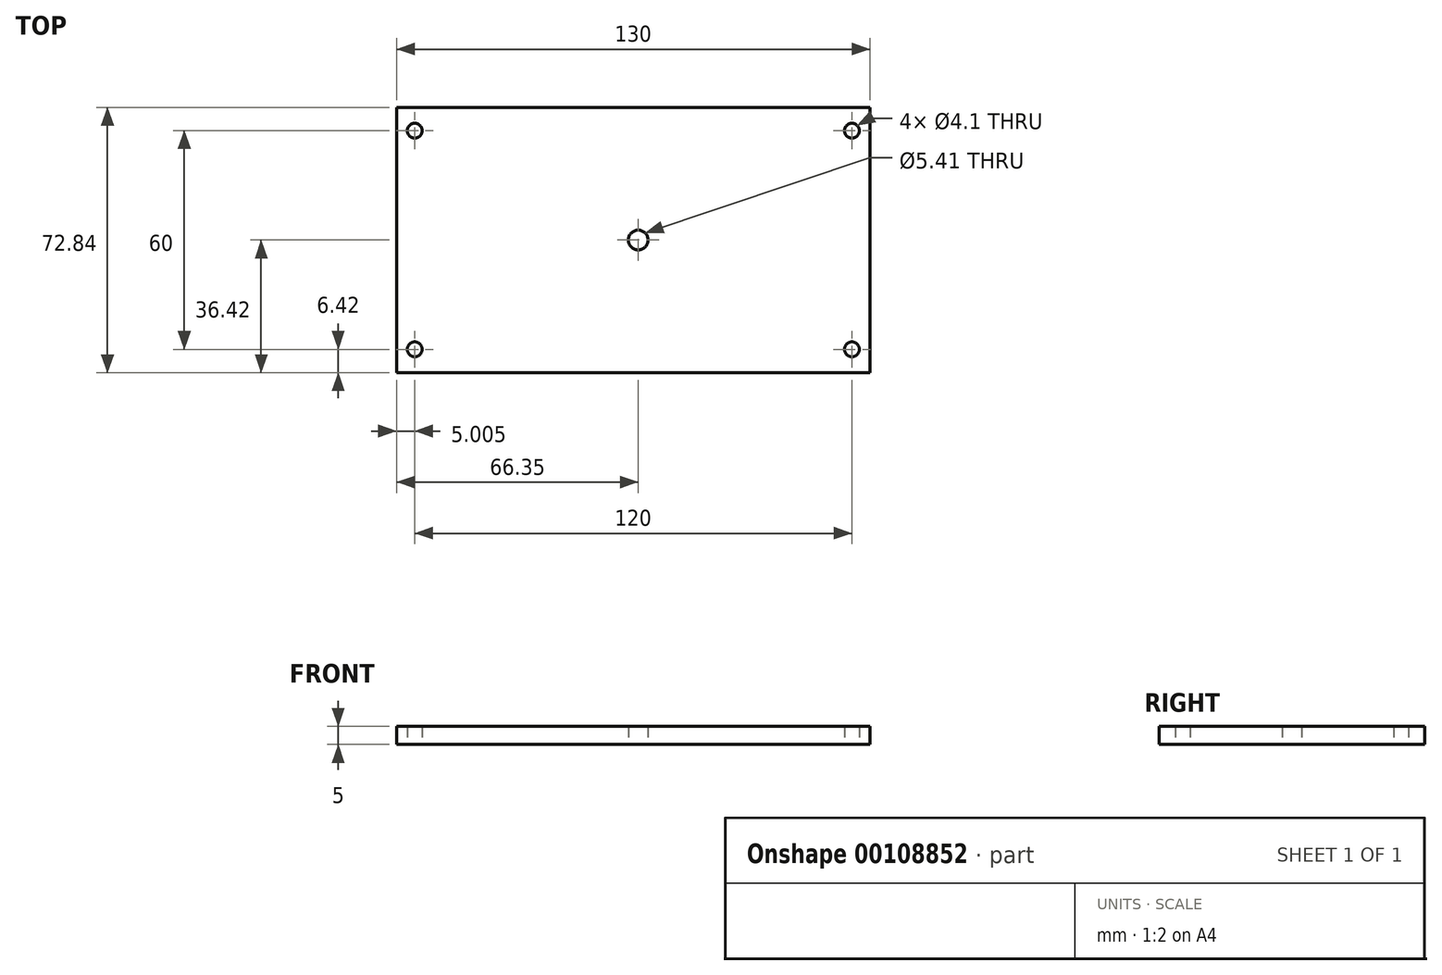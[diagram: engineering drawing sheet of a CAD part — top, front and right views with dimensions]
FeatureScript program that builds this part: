
annotation { "Feature Type Name" : "Feature", "Feature Type Description" : "" }
export const myFeature = defineFeature(function(context is Context, id is Id, definition is map)
    precondition{}
    {
        {
            var Q0;
            Q0=qCreatedBy(makeId("Top.planeOp"),FACE);
            var sketch = newSketch(context, id + "F0", { "sketchPlane" : qUnion([Q0])});
            skLineSegment(sketch, "E0", {"start": v(-72.88, 0) * mm, "end": v(75.67, 0) * mm, "construction": true});
            skLineSegment(sketch, "E1", {"start": v(0, 57.85) * mm, "end": v(0, -46.9) * mm, "construction": true});
            skLineSegment(sketch, "E2", {"start": v(-61.35, 34.24) * mm, "end": v(-61.35, -40.9) * mm, "construction": true});
            skLineSegment(sketch, "E3", {"start": v(58.65, 43.04) * mm, "end": v(58.65, -44.11) * mm, "construction": true});
            skLineSegment(sketch, "E4", {"start": v(-63.43, 30) * mm, "end": v(74.6, 30) * mm, "construction": true});
            skLineSegment(sketch, "E5", {"start": v(-63.43, -30) * mm, "end": v(67.94, -30) * mm, "construction": true});
            skPoint(sketch, "E6", {"position": v(-61.35, 30) * mm});
            skPoint(sketch, "E7", {"position": v(-61.35, -30) * mm});
            skPoint(sketch, "E8", {"position": v(58.65, -30) * mm});
            skPoint(sketch, "E9", {"position": v(58.65, 30) * mm});
            skLineSegment(sketch, "E10.bottom", {"start": v(-66.35, 0) * mm, "end": v(63.65, 0) * mm});
            skLineSegment(sketch, "E10.top", {"start": v(-66.35, 36.42) * mm, "end": v(63.65, 36.42) * mm});
            skLineSegment(sketch, "E10.left", {"start": v(-66.35, 0) * mm, "end": v(-66.35, 36.42) * mm});
            skLineSegment(sketch, "E10.right", {"start": v(63.65, 0) * mm, "end": v(63.65, 36.42) * mm});
            skLineSegment(sketch, "E11.MirrorCS", {"start": v(-66.35, -36.42) * mm, "end": v(63.65, -36.42) * mm});
            skLineSegment(sketch, "E12.MirrorCS", {"start": v(63.65, 0) * mm, "end": v(63.65, -36.42) * mm});
            skLineSegment(sketch, "E13.MirrorCS", {"start": v(-66.35, 0) * mm, "end": v(-66.35, -36.42) * mm});
            skPoint(sketch, "E14", {"position": v(0, 0) * mm});
            skSolve(sketch);
        }
        {
            var Q0;
            Q0 = qSketchRegion(id + "F0", true);
            extrude(context, id + "F1", {"entities" : qUnion([Q0]), "depth" : 5 * mm});
        }
        {
            var Q0;
            Q0=sQuery(id+"F0.wireOp",VERTEX,"E6");
            var Q1;
            Q1=sQuery(id+"F0.wireOp",VERTEX,"E7");
            var Q2;
            Q2=sQuery(id+"F0.wireOp",VERTEX,"E9");
            var Q3;
            Q3=sQuery(id+"F0.wireOp",VERTEX,"E8");
            var Q4;
            Q4=makeQuery(id+"F1.opExtrude","SWEPT_BODY",BODY,{"disambiguationData":[OSD([sQuery(id+"F0.wireOp",EDGE,"E10.top"),sQuery(id+"F0.wireOp",EDGE,"E10.left"),sQuery(id+"F0.wireOp",EDGE,"E10.right"),sQuery(id+"F0.wireOp",EDGE,"E11.MirrorCS"),sQuery(id+"F0.wireOp",EDGE,"E12.MirrorCS"),sQuery(id+"F0.wireOp",EDGE,"E13.MirrorCS")])]});
            hole(context, id + "F2", {"style" : HoleStyle.SIMPLE, "endStyle" : HoleEndStyle.THROUGH, "oppositeDirection" : true, "standardTappedOrClearance" : lookupTablePath({ "standard" : "ISO", "engagement" : "75%", "pitch" : "0.9 mm", "size" : "M5", "type" : "Tapped" }), "standardBlindInLast" : lookupTablePath({ "standard" : "ISO", "engagement" : "75%", "pitch" : "0.9 mm", "size" : "M5", "type" : "Tapped" }), "holeDiameter" : 4.1 * mm, "startFromSketch" : true, "locations" : qUnion([Q0, Q1, Q2, Q3]), "scope" : qUnion([Q4]), "isTappedThrough" : true, "showTappedDepth" : true});
        }
        {
            var Q0;
            Q0=sQuery(id+"F0.wireOp",VERTEX,"E14");
            var Q1;
            Q1=makeQuery(id+"F1.opExtrude","SWEPT_BODY",BODY,{"disambiguationData":[OSD([sQuery(id+"F0.wireOp",EDGE,"E10.top"),sQuery(id+"F0.wireOp",EDGE,"E10.left"),sQuery(id+"F0.wireOp",EDGE,"E10.right"),sQuery(id+"F0.wireOp",EDGE,"E11.MirrorCS"),sQuery(id+"F0.wireOp",EDGE,"E12.MirrorCS"),sQuery(id+"F0.wireOp",EDGE,"E13.MirrorCS")])]});
            hole(context, id + "F3", {"style" : HoleStyle.SIMPLE, "endStyle" : HoleEndStyle.THROUGH, "oppositeDirection" : true, "standardTappedOrClearance" : lookupTablePath({ "standard" : "ANSI", "engagement" : "75%", "pitch" : "28 tpi", "size" : "1/4", "type" : "Tapped" }), "standardBlindInLast" : lookupTablePath({ "standard" : "ANSI", "engagement" : "75%", "pitch" : "28 tpi", "size" : "1/4", "type" : "Tapped" }), "holeDiameter" : 5.4 * mm, "startFromSketch" : true, "locations" : qUnion([Q0]), "scope" : qUnion([Q1]), "isTappedThrough" : true, "majorDiameter" : 6.35 * mm, "showTappedDepth" : true});
        }
    });
